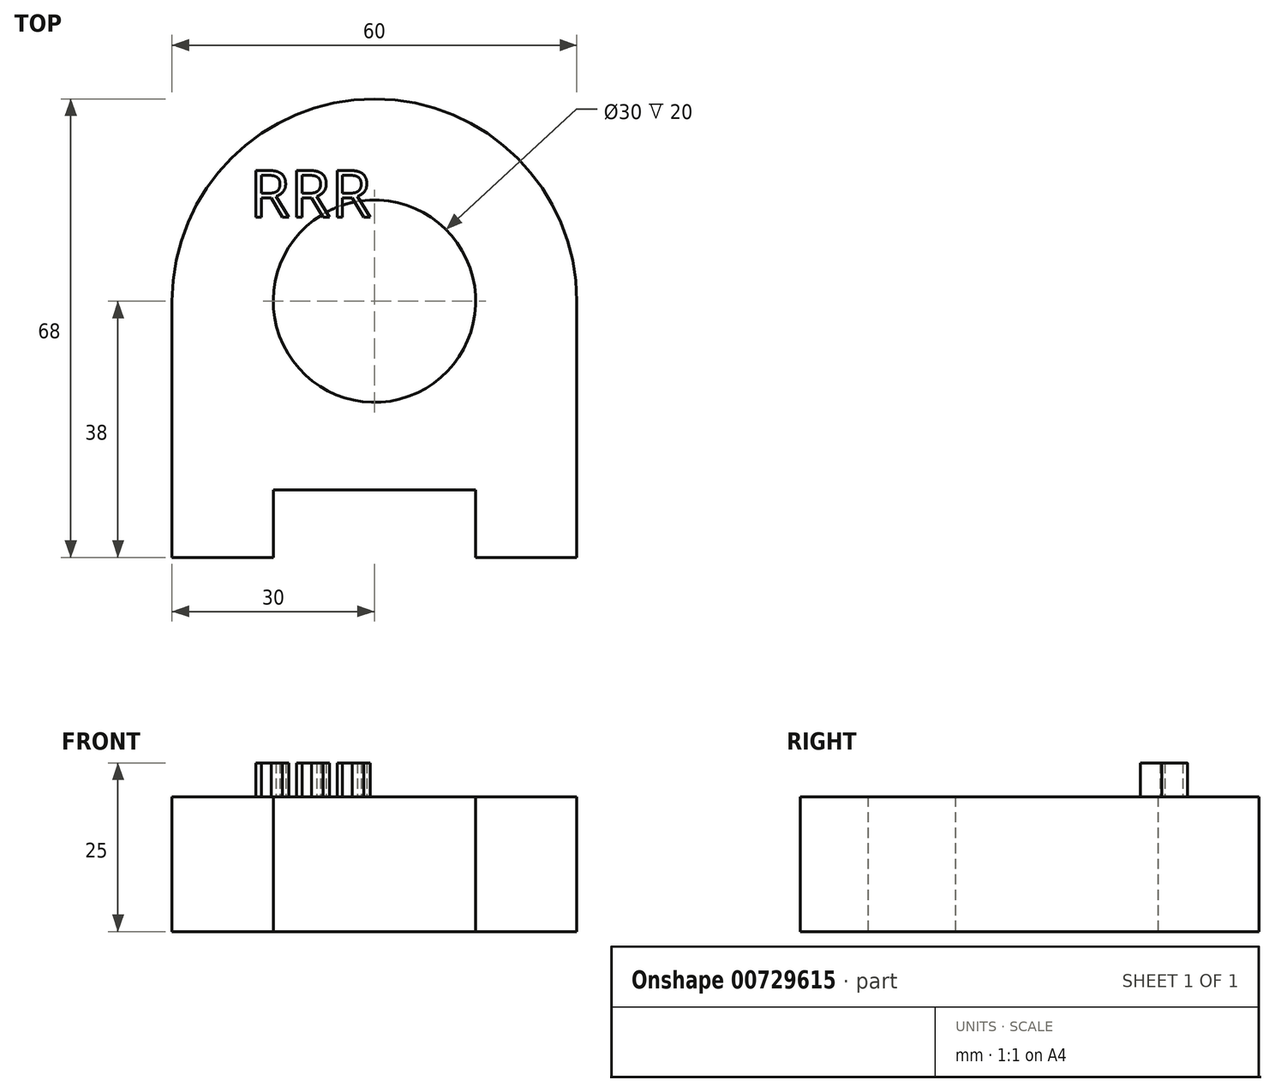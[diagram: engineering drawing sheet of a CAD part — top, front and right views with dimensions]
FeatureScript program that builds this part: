
annotation { "Feature Type Name" : "Feature", "Feature Type Description" : "" }
export const myFeature = defineFeature(function(context is Context, id is Id, definition is map)
    precondition{}
    {
        {
            var Q0;
            Q0=qCreatedBy(makeId("Top.planeOp"),FACE);
            var sketch = newSketch(context, id + "F0", { "sketchPlane" : qUnion([Q0])});
            skArc(sketch, "E0", {"start": v(30, 0) * mm, "mid": v(0, 30) * mm, "end": v(-30, 0) * mm});
            skCircle(sketch, "E1", {"center": v(0, 0) * mm, "radius": 15 * mm});
            skLineSegment(sketch, "E2", {"start": v(-30, 0) * mm, "end": v(-30, -38) * mm});
            skLineSegment(sketch, "E3", {"start": v(-30, -38) * mm, "end": v(-15, -38) * mm});
            skLineSegment(sketch, "E4", {"start": v(-15, -38) * mm, "end": v(-15, -28) * mm});
            skLineSegment(sketch, "E5", {"start": v(-15, -28) * mm, "end": v(15, -28) * mm});
            skLineSegment(sketch, "E6", {"start": v(15, -28) * mm, "end": v(15, -38) * mm});
            skLineSegment(sketch, "E7", {"start": v(30, 0) * mm, "end": v(30, -38) * mm});
            skLineSegment(sketch, "E8", {"start": v(30, -38) * mm, "end": v(15, -38) * mm});
            skSolve(sketch);
        }
        {
            var Q0;
            Q0=makeQuery(id+"F0.imprint","IMPRINT",FACE,{"disambiguationData":[TD([[makeQuery(id+"F0.imprint","IMPRINT",EDGE,{"derivedFrom":sQuery(id+"F0.wireOp",EDGE,"E0")}),1.0]])]});
            extrude(context, id + "F1", {"entities" : qUnion([Q0]), "depth" : 20 * mm, "offsetDistance" : 25 * mm});
        }
        {
            var Q0;
            Q0=makeQuery(id+"F1.opExtrude","CAP_FACE",FACE,{"disambiguationData":[OSD([sQuery(id+"F0.wireOp",EDGE,"E0"),sQuery(id+"F0.wireOp",EDGE,"E1"),sQuery(id+"F0.wireOp",EDGE,"E2"),sQuery(id+"F0.wireOp",EDGE,"E3"),sQuery(id+"F0.wireOp",EDGE,"E4"),sQuery(id+"F0.wireOp",EDGE,"E5"),sQuery(id+"F0.wireOp",EDGE,"E6"),sQuery(id+"F0.wireOp",EDGE,"E7"),sQuery(id+"F0.wireOp",EDGE,"E8")])],"isStart":false});
            var sketch = newSketch(context, id + "F2", { "sketchPlane" : qUnion([Q0])});
            skText(sketch, "E9", { "text": "RRR", "fontName": "OpenSans-Regular.ttf"});
            const initialGuessF2  = {"E9": [-0.01853, 0.01243, 1, 0, 0.00701]};
            skSetInitialGuess(sketch, initialGuessF2);
            skSolve(sketch);
        }
        {
            var Q0;
            Q0 = qSketchRegion(id + "F2", true);
            extrude(context, id + "F3", {"entities" : qUnion([Q0]), "operationType" : NewBodyOperationType.ADD, "depth" : 5 * mm, "offsetDistance" : 25 * mm});
        }
    });
